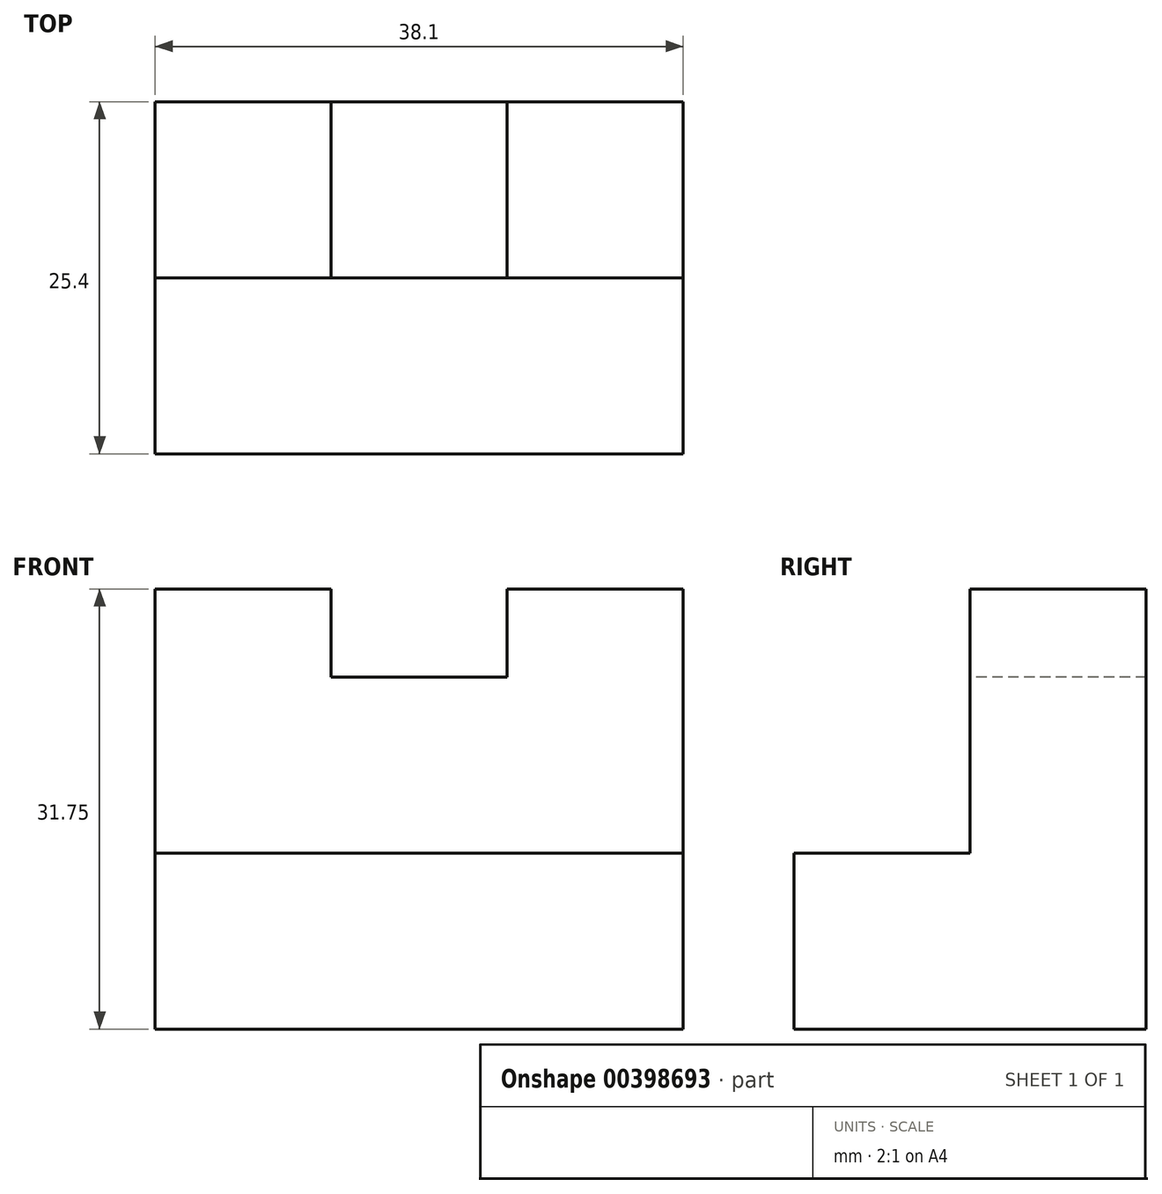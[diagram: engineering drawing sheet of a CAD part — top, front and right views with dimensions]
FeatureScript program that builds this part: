
annotation { "Feature Type Name" : "Feature", "Feature Type Description" : "" }
export const myFeature = defineFeature(function(context is Context, id is Id, definition is map)
    precondition{}
    {
        {
            var Q0;
            Q0=qCreatedBy(makeId("Right.planeOp"),FACE);
            var sketch = newSketch(context, id + "F0", { "sketchPlane" : qUnion([Q0])});
            skLineSegment(sketch, "E0", {"start": v(0, 0) * mm, "end": v(0, 31.75) * mm});
            skLineSegment(sketch, "E1", {"start": v(0, 31.75) * mm, "end": v(-12.7, 31.75) * mm});
            skLineSegment(sketch, "E2", {"start": v(-12.7, 31.75) * mm, "end": v(-12.7, 12.7) * mm});
            skLineSegment(sketch, "E3", {"start": v(-12.7, 12.7) * mm, "end": v(-25.4, 12.7) * mm});
            skLineSegment(sketch, "E4", {"start": v(-25.4, 12.7) * mm, "end": v(-25.4, 0) * mm});
            skLineSegment(sketch, "E5", {"start": v(-25.4, 0) * mm, "end": v(0, 0) * mm});
            skSolve(sketch);
        }
        {
            var Q0;
            Q0=qSketchRegion(id+"F0",true);
            extrude(context, id + "F1", {"entities" : qUnion([Q0]), "depth" : 38.1 * mm});
        }
        {
            var Q0;
            Q0=makeQuery(id+"F1.opExtrude","SWEPT_FACE",FACE,{"disambiguationData":[OSD([sQuery(id+"F0.wireOp",EDGE,"E2")])]});
            var sketch = newSketch(context, id + "F2", { "sketchPlane" : qUnion([Q0])});
            skLineSegment(sketch, "E6", {"start": v(12.7, 31.75) * mm, "end": v(12.7, 25.4) * mm});
            skLineSegment(sketch, "E7", {"start": v(12.7, 25.4) * mm, "end": v(25.4, 25.4) * mm});
            skLineSegment(sketch, "E8", {"start": v(25.4, 25.4) * mm, "end": v(25.4, 31.75) * mm});
            skSolve(sketch);
        }
        {
            var Q0;
            {var subQ0=sQuery(id+"F2.wireOp",EDGE,"E6");Q0=makeQuery(id+"F2.imprint","IMPRINT",FACE,{"disambiguationData":[TD([[makeQuery(id+"F2.imprint","IMPRINT",EDGE,{"derivedFrom":subQ0}),1.0]])]});}
            extrude(context, id + "F3", {"entities" : qUnion([Q0]), "operationType" : NewBodyOperationType.REMOVE, "oppositeDirection" : true, "depth" : 12.7 * mm});
        }
    });
